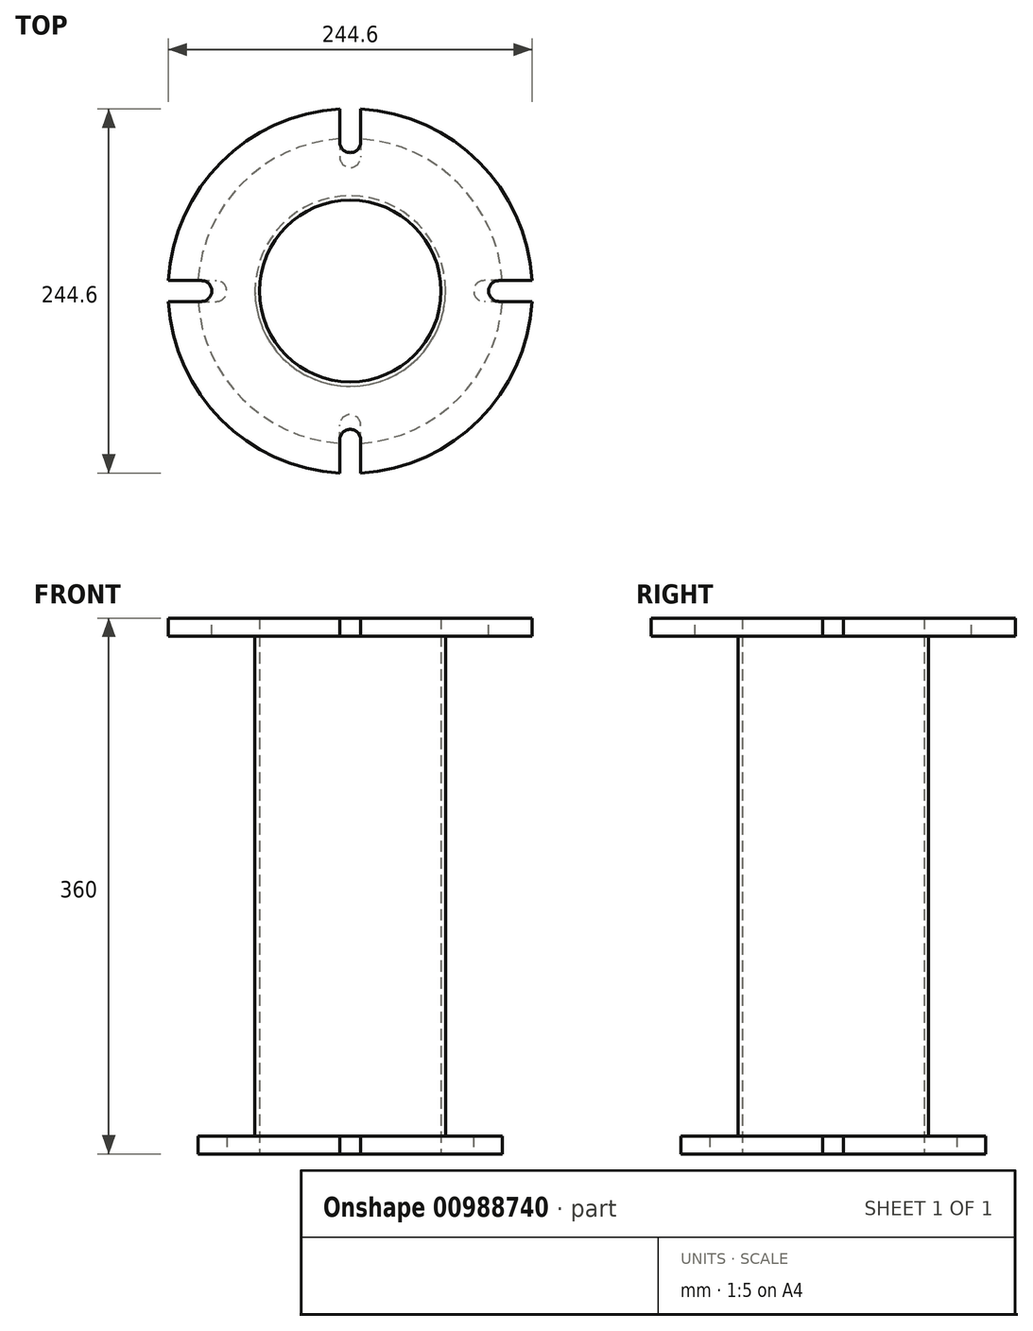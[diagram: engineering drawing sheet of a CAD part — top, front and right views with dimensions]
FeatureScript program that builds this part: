
annotation { "Feature Type Name" : "Feature", "Feature Type Description" : "" }
export const myFeature = defineFeature(function(context is Context, id is Id, definition is map)
    precondition{}
    {
        {
            var Q0;
            Q0=qCreatedBy(makeId("Top.planeOp"),FACE);
            var sketch = newSketch(context, id + "F0", { "sketchPlane" : qUnion([Q0])});
            skCircle(sketch, "E0", {"center": v(0, 0) * mm, "radius": 64 * mm});
            skCircle(sketch, "E1", {"center": v(0, 0) * mm, "radius": 61 * mm});
            skSolve(sketch);
        }
        {
            var Q0;
            Q0 = qSketchRegion(id + "F0", true);
            extrude(context, id + "F1", {"entities" : qUnion([Q0]), "depth" : 360 * mm, "offsetDistance" : 25 * mm});
        }
        {
            var Q0;
            Q0=makeQuery(id+"F1.opExtrude","CAP_FACE",FACE,{"disambiguationData":[OSD([sQuery(id+"F0.wireOp",EDGE,"E0"),sQuery(id+"F0.wireOp",EDGE,"E1")])],"isStart":false});
            var sketch = newSketch(context, id + "F2", { "sketchPlane" : qUnion([Q0])});
            skCircle(sketch, "E2", {"center": v(0, 0) * mm, "radius": 64 * mm});
            skArc(sketch, "E3", {"start": v(-122.3, -7) * mm, "mid": v(-86.62, -86.62) * mm, "end": v(-7, -122.3) * mm});
            skLineSegment(sketch, "E4", {"start": v(-7, 122.3) * mm, "end": v(-7, 100) * mm});
            skLineSegment(sketch, "E5", {"start": v(7, 122.3) * mm, "end": v(7, 100) * mm});
            skArc(sketch, "E6", {"start": v(-7, 100) * mm, "mid": v(0, 93) * mm, "end": v(7, 100) * mm});
            skLineSegment(sketch, "E7.1.0", {"start": v(-122.3, 7) * mm, "end": v(-100, 7) * mm});
            skLineSegment(sketch, "E7.1.1", {"start": v(-122.3, -7) * mm, "end": v(-100, -7) * mm});
            skArc(sketch, "E7.1.2", {"start": v(-100, -7) * mm, "mid": v(-93, 0) * mm, "end": v(-100, 7) * mm});
            skLineSegment(sketch, "E7.2.0", {"start": v(-7, -122.3) * mm, "end": v(-7, -100) * mm});
            skLineSegment(sketch, "E7.2.1", {"start": v(7, -122.3) * mm, "end": v(7, -100) * mm});
            skArc(sketch, "E7.2.2", {"start": v(7, -100) * mm, "mid": v(0, -93) * mm, "end": v(-7, -100) * mm});
            skLineSegment(sketch, "E7.3.0", {"start": v(122.3, -7) * mm, "end": v(100, -7) * mm});
            skLineSegment(sketch, "E7.3.1", {"start": v(122.3, 7) * mm, "end": v(100, 7) * mm});
            skArc(sketch, "E7.3.2", {"start": v(100, 7) * mm, "mid": v(93, 0) * mm, "end": v(100, -7) * mm});
            skArc(sketch, "E8.trimOffspring", {"start": v(-7, 122.3) * mm, "mid": v(-86.62, 86.62) * mm, "end": v(-122.3, 7) * mm});
            skArc(sketch, "E9.trimOffspring", {"start": v(122.3, 7) * mm, "mid": v(86.62, 86.62) * mm, "end": v(7, 122.3) * mm});
            skArc(sketch, "E10.trimOffspring", {"start": v(7, -122.3) * mm, "mid": v(86.62, -86.62) * mm, "end": v(122.3, -7) * mm});
            skSolve(sketch);
        }
        {
            var Q0;
            Q0 = qSketchRegion(id + "F2", true);
            extrude(context, id + "F3", {"entities" : qUnion([Q0]), "operationType" : NewBodyOperationType.ADD, "oppositeDirection" : true, "depth" : 12 * mm, "offsetDistance" : 25 * mm});
        }
        {
            var Q0;
            Q0=makeQuery(id+"F1.opExtrude","CAP_FACE",FACE,{"disambiguationData":[OSD([sQuery(id+"F0.wireOp",EDGE,"E0"),sQuery(id+"F0.wireOp",EDGE,"E1")])],"isStart":true});
            var sketch = newSketch(context, id + "F4", { "sketchPlane" : qUnion([Q0])});
            skCircle(sketch, "E11", {"center": v(0, 0) * mm, "radius": 64 * mm});
            skArc(sketch, "E12", {"start": v(-7, 102.26) * mm, "mid": v(-72.48, 72.48) * mm, "end": v(-102.26, 7) * mm});
            skLineSegment(sketch, "E13", {"start": v(-7, 102.26) * mm, "end": v(-7, 90) * mm});
            skLineSegment(sketch, "E14", {"start": v(7, 102.26) * mm, "end": v(7, 90) * mm});
            skArc(sketch, "E15", {"start": v(-7, 90) * mm, "mid": v(0, 83) * mm, "end": v(7, 90) * mm});
            skLineSegment(sketch, "E16.1.0", {"start": v(-102.26, 7) * mm, "end": v(-90, 7) * mm});
            skLineSegment(sketch, "E16.1.1", {"start": v(-102.26, -7) * mm, "end": v(-90, -7) * mm});
            skArc(sketch, "E16.1.2", {"start": v(-90, -7) * mm, "mid": v(-83, 0) * mm, "end": v(-90, 7) * mm});
            skLineSegment(sketch, "E16.2.0", {"start": v(-7, -102.26) * mm, "end": v(-7, -90) * mm});
            skLineSegment(sketch, "E16.2.1", {"start": v(7, -102.26) * mm, "end": v(7, -90) * mm});
            skArc(sketch, "E16.2.2", {"start": v(7, -90) * mm, "mid": v(0, -83) * mm, "end": v(-7, -90) * mm});
            skLineSegment(sketch, "E16.3.0", {"start": v(102.26, -7) * mm, "end": v(90, -7) * mm});
            skLineSegment(sketch, "E16.3.1", {"start": v(102.26, 7) * mm, "end": v(90, 7) * mm});
            skArc(sketch, "E16.3.2", {"start": v(90, 7) * mm, "mid": v(83, 0) * mm, "end": v(90, -7) * mm});
            skArc(sketch, "E17.trimOffspring", {"start": v(-102.26, -7) * mm, "mid": v(-72.48, -72.48) * mm, "end": v(-7, -102.26) * mm});
            skArc(sketch, "E18.trimOffspring", {"start": v(7, -102.26) * mm, "mid": v(72.48, -72.48) * mm, "end": v(102.26, -7) * mm});
            skArc(sketch, "E19.trimOffspring", {"start": v(102.26, 7) * mm, "mid": v(72.48, 72.48) * mm, "end": v(7, 102.26) * mm});
            skSolve(sketch);
        }
        {
            var Q0;
            Q0 = qSketchRegion(id + "F4", true);
            extrude(context, id + "F5", {"entities" : qUnion([Q0]), "operationType" : NewBodyOperationType.ADD, "oppositeDirection" : true, "depth" : 12 * mm, "offsetDistance" : 25 * mm});
        }
    });
